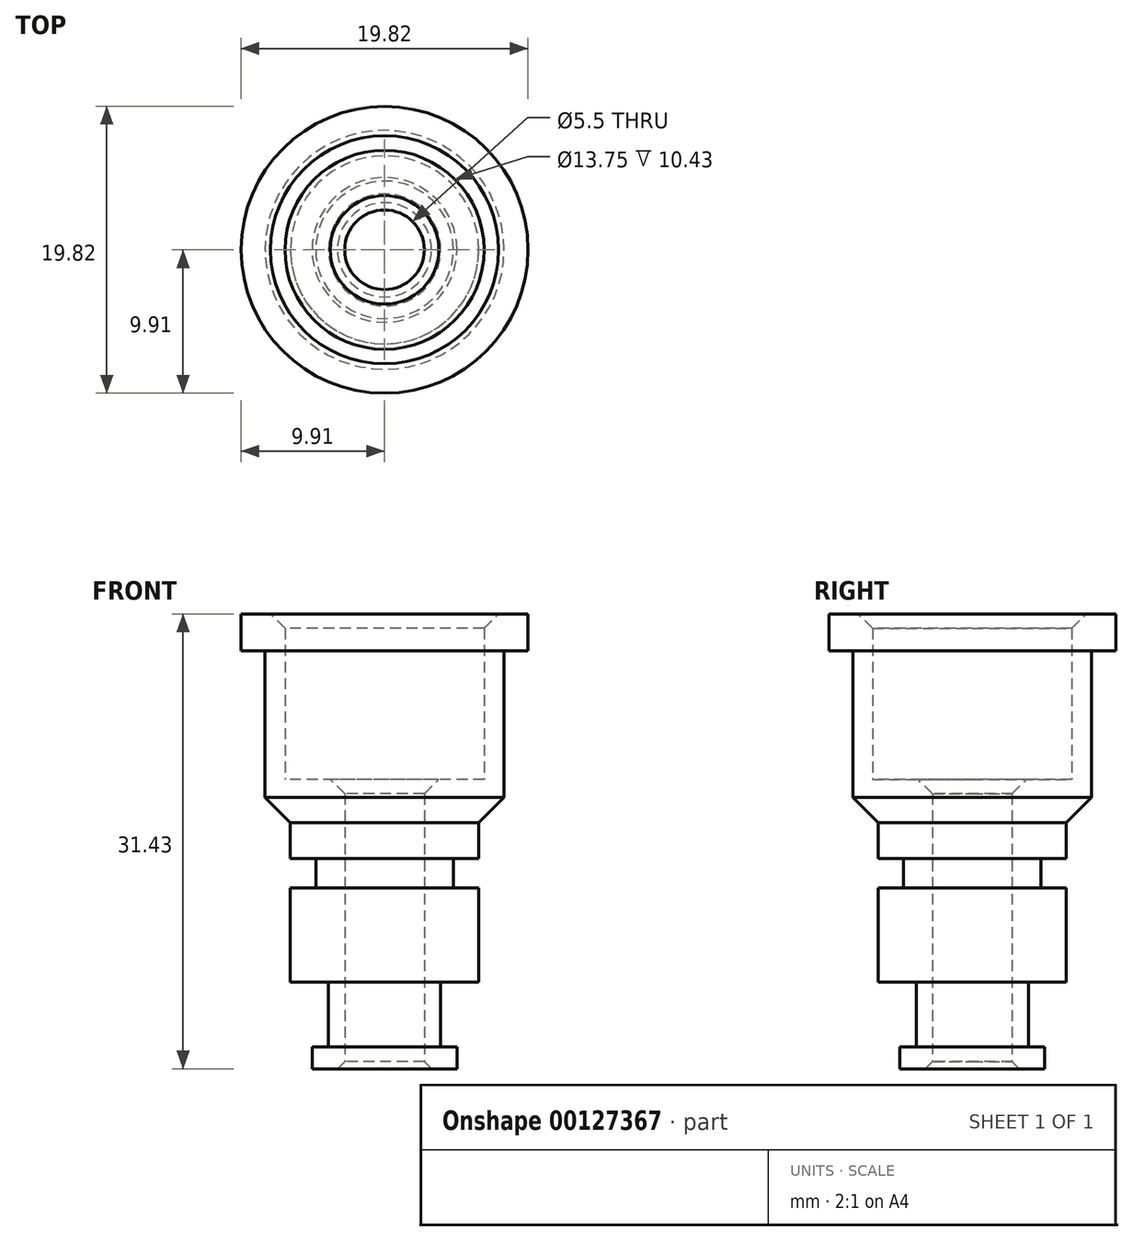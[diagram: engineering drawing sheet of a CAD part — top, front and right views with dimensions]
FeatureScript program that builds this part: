
annotation { "Feature Type Name" : "Feature", "Feature Type Description" : "" }
export const myFeature = defineFeature(function(context is Context, id is Id, definition is map)
    precondition{}
    {
        {
            var Q0;
            Q0=qCreatedBy(makeId("Top.planeOp"),FACE);
            var sketch = newSketch(context, id + "F0", { "sketchPlane" : qUnion([Q0])});
            skCircle(sketch, "E0", {"center": v(0, 0) * mm, "radius": 6.5 * mm});
            skCircle(sketch, "E1", {"center": v(0, 0) * mm, "radius": 2.75 * mm});
            skSolve(sketch);
        }
        {
            var Q0;
            Q0=qSketchRegion(id+"F0",true);
            extrude(context, id + "F1", {"entities" : qUnion([Q0]), "depth" : 20 * mm});
        }
        {
            var Q0;
            Q0=makeQuery(id+"F1.opExtrude","CAP_FACE",FACE,{"disambiguationData":[OSD([sQuery(id+"F0.wireOp",EDGE,"E0"),sQuery(id+"F0.wireOp",EDGE,"E1")])],"isStart":true});
            var sketch = newSketch(context, id + "F2", { "sketchPlane" : qUnion([Q0])});
            skCircle(sketch, "E2.0", {"center": v(0, 0) * mm, "radius": 6.5 * mm});
            skCircle(sketch, "E3", {"center": v(0, 0) * mm, "radius": 5 * mm});
            skSolve(sketch);
        }
        {
            var Q0;
            Q0=qSketchRegion(id+"F2",true);
            extrude(context, id + "F3", {"entities" : qUnion([Q0]), "operationType" : NewBodyOperationType.REMOVE, "oppositeDirection" : true, "depth" : 6 * mm});
        }
        {
            var Q0;
            Q0=makeQuery(id+"F3.boolean.opBoolean","COPY",FACE,{"derivedFrom":makeQuery(id+"F3.opExtrude","CAP_FACE",FACE,{"disambiguationData":[OSD([sQuery(id+"F2.wireOp",EDGE,"E2.0"),sQuery(id+"F2.wireOp",EDGE,"E3")])],"isStart":false})});
            var sketch = newSketch(context, id + "F4", { "sketchPlane" : qUnion([Q0])});
            skCircle(sketch, "E4.0", {"center": v(0, 0) * mm, "radius": 5 * mm});
            skCircle(sketch, "E5", {"center": v(0, 0) * mm, "radius": 3.88 * mm});
            skSolve(sketch);
        }
        {
            var Q0;
            Q0=qSketchRegion(id+"F4",true);
            extrude(context, id + "F5", {"entities" : qUnion([Q0]), "operationType" : NewBodyOperationType.REMOVE, "depth" : 4.5 * mm});
        }
        {
            var Q0;
            Q0=makeQuery(id+"F1.opExtrude","CAP_FACE",FACE,{"disambiguationData":[OSD([sQuery(id+"F0.wireOp",EDGE,"E0"),sQuery(id+"F0.wireOp",EDGE,"E1")])],"isStart":true});
            cPlane(context, id + "F6", {"entities" : qUnion([Q0]), "cplaneType" : CPlaneType.OFFSET, "offset" : 12.5 * mm, "oppositeDirection" : true, "width" : 150 * mm, "height" : 150 * mm});
        }
        {
            var Q0;
            Q0=qCreatedBy(id+"F6.planeOp",FACE);
            var sketch = newSketch(context, id + "F7", { "sketchPlane" : qUnion([Q0])});
            skCircle(sketch, "E6.0", {"center": v(0, 0) * mm, "radius": 6.5 * mm});
            skCircle(sketch, "E7", {"center": v(0, 0) * mm, "radius": 4.75 * mm});
            skSolve(sketch);
        }
        {
            var Q0;
            Q0=qSketchRegion(id+"F7",true);
            extrude(context, id + "F8", {"entities" : qUnion([Q0]), "operationType" : NewBodyOperationType.REMOVE, "oppositeDirection" : true, "depth" : 2.03 * mm});
        }
        {
            var Q0;
            Q0=makeQuery(id+"F1.opExtrude","CAP_FACE",FACE,{"disambiguationData":[OSD([sQuery(id+"F0.wireOp",EDGE,"E0"),sQuery(id+"F0.wireOp",EDGE,"E1")])],"isStart":false});
            var sketch = newSketch(context, id + "F9", { "sketchPlane" : qUnion([Q0])});
            skCircle(sketch, "E8.0", {"center": v(0, 0) * mm, "radius": 6.5 * mm});
            skCircle(sketch, "E9", {"center": v(0, 0) * mm, "radius": 8.25 * mm});
            skSolve(sketch);
        }
        {
            var Q0;
            Q0=qSketchRegion(id+"F9",true);
            extrude(context, id + "F10", {"entities" : qUnion([Q0]), "operationType" : NewBodyOperationType.ADD, "oppositeDirection" : true, "depth" : 3 * mm});
        }
        {
            var Q0;
            Q0=makeQuery(id+"F10.boolean.opBoolean","MERGE",FACE,{"derivedFrom":[makeQuery(id+"F1.opExtrude","CAP_FACE",FACE,{"disambiguationData":[OSD([sQuery(id+"F0.wireOp",EDGE,"E0"),sQuery(id+"F0.wireOp",EDGE,"E1")])],"isStart":false}),makeQuery(id+"F10.opExtrude","CAP_FACE",FACE,{"disambiguationData":[OSD([sQuery(id+"F9.wireOp",EDGE,"E8.0"),sQuery(id+"F9.wireOp",EDGE,"E9")])],"isStart":true})]});
            var sketch = newSketch(context, id + "F11", { "sketchPlane" : qUnion([Q0])});
            skCircle(sketch, "E10", {"center": v(0, 0) * mm, "radius": 6.88 * mm});
            skCircle(sketch, "E11.0", {"center": v(0, 0) * mm, "radius": 8.25 * mm});
            skSolve(sketch);
        }
        {
            var Q0;
            Q0=qSketchRegion(id+"F11",true);
            extrude(context, id + "F12", {"entities" : qUnion([Q0]), "operationType" : NewBodyOperationType.ADD, "depth" : 11.43 * mm});
        }
        {
            var Q0;
            Q0=makeQuery(id+"F12.opExtrude","CAP_FACE",FACE,{"disambiguationData":[OSD([sQuery(id+"F11.wireOp",EDGE,"E10"),sQuery(id+"F11.wireOp",EDGE,"E11.0")])],"isStart":false});
            var sketch = newSketch(context, id + "F13", { "sketchPlane" : qUnion([Q0])});
            skCircle(sketch, "E12.0", {"center": v(0, 0) * mm, "radius": 8.25 * mm});
            skCircle(sketch, "E13", {"center": v(0, 0) * mm, "radius": 9.9 * mm});
            skSolve(sketch);
        }
        {
            var Q0;
            Q0=qSketchRegion(id+"F13",true);
            extrude(context, id + "F14", {"entities" : qUnion([Q0]), "operationType" : NewBodyOperationType.ADD, "oppositeDirection" : true, "depth" : 2.54 * mm});
        }
        {
            var Q0;
            Q0=makeQuery(id+"F10.opExtrude","CAP_EDGE",EDGE,{"disambiguationData":[OSD([sQuery(id+"F9.wireOp",EDGE,"E9")])],"isStart":false});
            chamfer(context, id + "F15", {"entities" : qUnion([Q0]), "width" : 1.75 * mm, "tangentPropagation" : true});
        }
        {
            var Q0;
            Q0=makeQuery(id+"F12.opExtrude","CAP_EDGE",EDGE,{"disambiguationData":[OSD([sQuery(id+"F11.wireOp",EDGE,"E10")])],"isStart":false});
            chamfer(context, id + "F16", {"entities" : qUnion([Q0]), "width" : 1 * mm, "tangentPropagation" : true});
        }
        {
            var Q0;
            Q0=makeQuery(id+"F1.opExtrude","CAP_EDGE",EDGE,{"disambiguationData":[OSD([sQuery(id+"F0.wireOp",EDGE,"E1")])],"isStart":true});
            chamfer(context, id + "F17", {"entities" : qUnion([Q0]), "width" : .5 * mm, "tangentPropagation" : true});
        }
        {
            var Q0;
            Q0=makeQuery(id+"F1.opExtrude","CAP_EDGE",EDGE,{"disambiguationData":[OSD([sQuery(id+"F0.wireOp",EDGE,"E1")])],"isStart":false});
            chamfer(context, id + "F18", {"entities" : qUnion([Q0]), "width" : 1 * mm, "tangentPropagation" : true});
        }
    });
